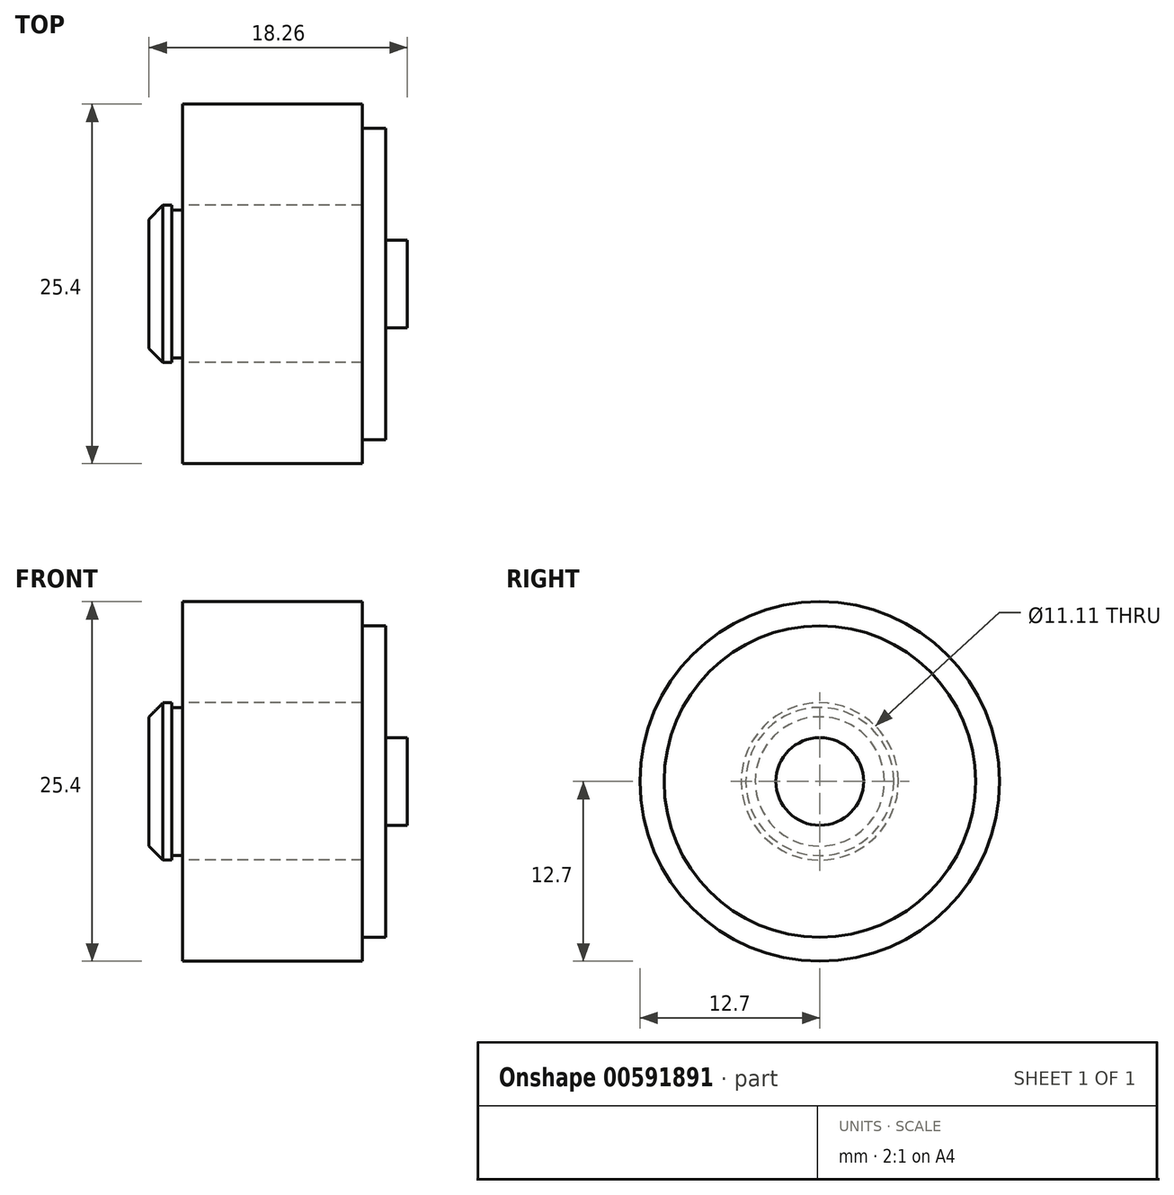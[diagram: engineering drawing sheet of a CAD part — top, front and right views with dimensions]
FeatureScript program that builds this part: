
annotation { "Feature Type Name" : "Feature", "Feature Type Description" : "" }
export const myFeature = defineFeature(function(context is Context, id is Id, definition is map)
    precondition{}
    {
        {
            var Q0;
            Q0=qCreatedBy(makeId("Front.planeOp"),FACE);
            var sketch = newSketch(context, id + "F0", { "sketchPlane" : qUnion([Q0])});
            skLineSegment(sketch, "E0", {"start": v(0, 0) * mm, "end": v(0, 3.1) * mm});
            skLineSegment(sketch, "E1", {"start": v(0, 3.1) * mm, "end": v(-1.52, 3.1) * mm});
            skLineSegment(sketch, "E2", {"start": v(-1.52, 3.1) * mm, "end": v(-1.52, 11) * mm});
            skLineSegment(sketch, "E3", {"start": v(-1.52, 11) * mm, "end": v(-3.2, 11) * mm});
            skLineSegment(sketch, "E4", {"start": v(-3.2, 11) * mm, "end": v(-3.2, 5.55) * mm});
            skLineSegment(sketch, "E5", {"start": v(-3.2, 5.56) * mm, "end": v(-15.9, 5.55) * mm});
            skLineSegment(sketch, "E6", {"start": v(-15.9, 5.55) * mm, "end": v(-15.9, 5.23) * mm});
            skLineSegment(sketch, "E7", {"start": v(-15.9, 5.23) * mm, "end": v(-16.66, 5.23) * mm});
            skLineSegment(sketch, "E8", {"start": v(-16.66, 5.23) * mm, "end": v(-16.66, 5.55) * mm});
            skLineSegment(sketch, "E9", {"start": v(-16.66, 5.55) * mm, "end": v(-17.27, 5.55) * mm});
            skLineSegment(sketch, "E10", {"start": v(-17.27, 5.56) * mm, "end": v(-18.26, 4.56) * mm});
            skLineSegment(sketch, "E11", {"start": v(-18.26, 4.56) * mm, "end": v(-18.26, 0) * mm});
            skLineSegment(sketch, "E12", {"start": v(-18.26, 0) * mm, "end": v(0, 0) * mm});
            skLineSegment(sketch, "E13", {"start": v(-9.55, 5.55) * mm, "end": v(-9.55, 0) * mm, "construction": true});
            skLineSegment(sketch, "E14", {"start": v(-18.26, 4.56) * mm, "end": v(-18.26, 5.55) * mm, "construction": true});
            skLineSegment(sketch, "E15", {"start": v(-18.26, 5.55) * mm, "end": v(-17.27, 5.55) * mm, "construction": true});
            skLineSegment(sketch, "E16", {"start": v(-16.28, 5.23) * mm, "end": v(-16.28, 0) * mm, "construction": true});
            skLineSegment(sketch, "E17.bottom", {"start": v(-3.2, 5.55) * mm, "end": v(-15.9, 5.55) * mm});
            skLineSegment(sketch, "E17.top", {"start": v(-3.2, 12.7) * mm, "end": v(-15.9, 12.7) * mm});
            skLineSegment(sketch, "E17.left", {"start": v(-3.2, 5.55) * mm, "end": v(-3.2, 12.7) * mm});
            skLineSegment(sketch, "E17.right", {"start": v(-15.9, 5.55) * mm, "end": v(-15.9, 12.7) * mm});
            skSolve(sketch);
        }
        {
            var Q0;
            Q0=makeQuery(id+"F0.imprint","IMPRINT",FACE,{"disambiguationData":[TD([[makeQuery(id+"F0.imprint","IMPRINT",EDGE,{"derivedFrom":sQuery(id+"F0.wireOp",EDGE,"E0")}),1.0]])]});
            var Q1;
            Q1=sQuery(id+"F0.wireOp",EDGE,"E12");
            revolve(context, id + "F1", {"surfaceOperationType" : NewSurfaceOperationType.NEW, "entities" : qUnion([Q0]), "axis" : qUnion([Q1]), "revolveType" : RevolveType.FULL});
        }
        {
            var Q0;
            {var subQ7=sQuery(id+"F0.wireOp",EDGE,"E17.top");Q0=makeQuery(id+"F0.imprint","IMPRINT",FACE,{"disambiguationData":[TD([[makeQuery(id+"F0.imprint","IMPRINT",EDGE,{"derivedFrom":subQ7}),1.0]])]});}
            var Q1;
            Q1=sQuery(id+"F0.wireOp",EDGE,"E12");
            revolve(context, id + "F2", {"surfaceOperationType" : NewSurfaceOperationType.NEW, "entities" : qUnion([Q0]), "axis" : qUnion([Q1]), "revolveType" : RevolveType.FULL});
        }
    });
